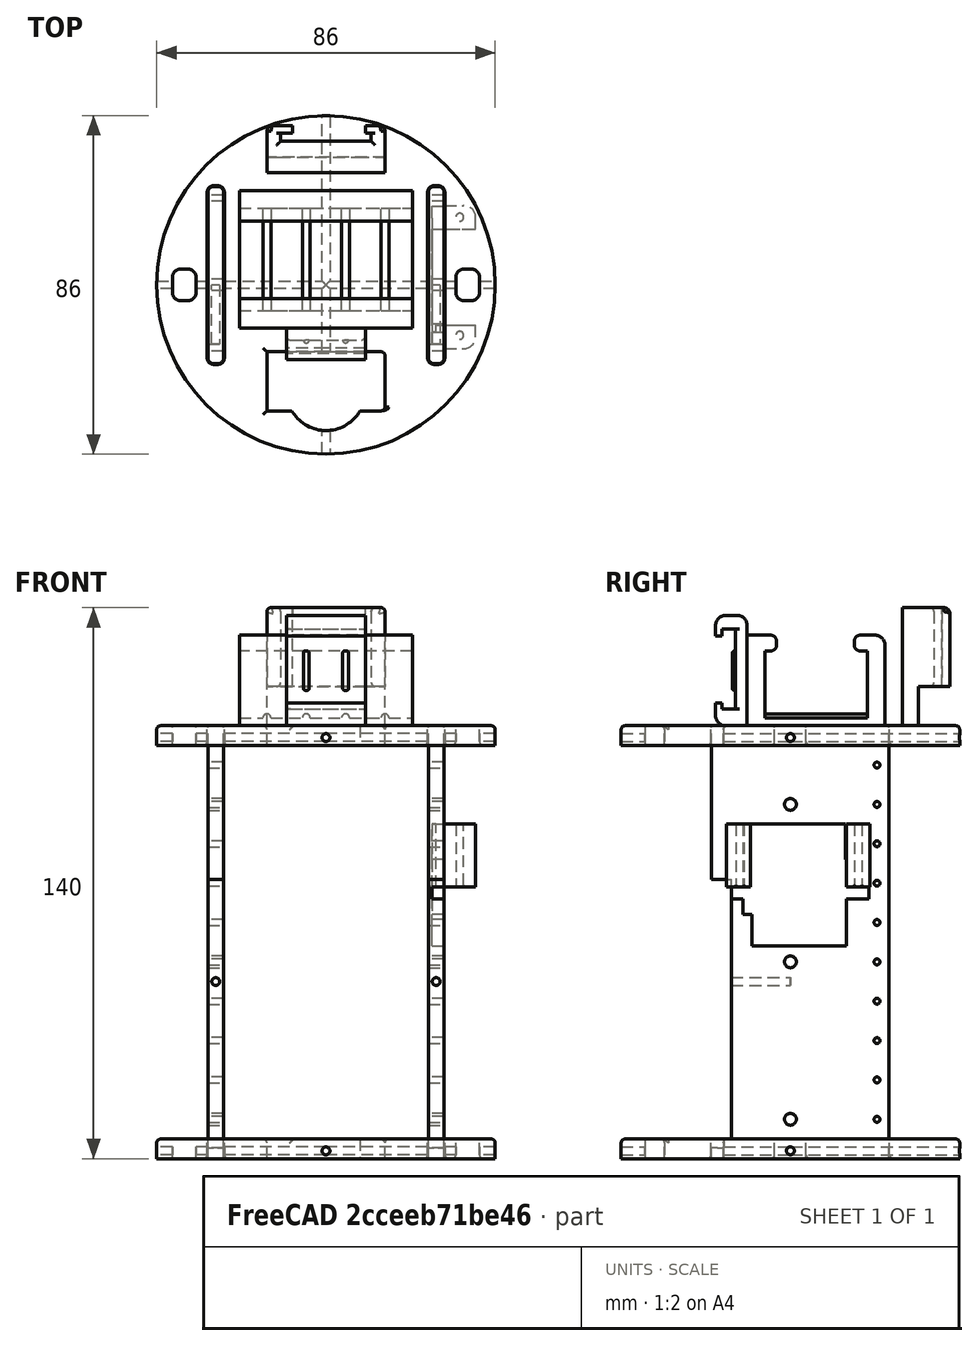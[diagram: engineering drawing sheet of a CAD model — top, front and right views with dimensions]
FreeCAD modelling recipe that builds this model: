
FCSTD DOCUMENT  (FreeCAD 1.0R39109 (Git))
Label: Base_superior_capsula
License: All rights reserved
LicenseURL: http://en.wikipedia.org/wiki/All_rights_reserved
objects: Part::Cut×130, Part::Cylinder×98, Part::Fillet×96, Part::Box×72, Part::MultiFuse×37, Part::Offset×12, Part::Chamfer×1
note: 446 computed .brp shape members not serialized (recipe doc carries the construction recipe); baked Part::Feature solids carry a one-line shape summary decoded from their .brp

FEATURE [Part::Box] Box  label="Extensor"
  AttacherType = Attacher::AttachEngine3D
  Height = 66
  Length = 11
  Placement = pos=(30,-28,3) rot=(0,0,1;1.5708rad)
  Width = 60
FEATURE [Part::Box] Box001  label="Cubo001"
  AttacherType = Attacher::AttachEngine3D
  Height = 110
  Length = 45
  Placement = pos=(-30,25,0) rot=(0,0,-1;1.5708rad)
  Width = 4
FEATURE [Part::Box] Box002  label="Cubo002"
  AttacherType = Attacher::AttachEngine3D
  Height = 110
  Length = 45
  Placement = pos=(-30,25,0) rot=(0,0,-1;1.5708rad)
  Width = 4
FEATURE [Part::Box] Box003  label="Cubo003"
  AttacherType = Attacher::AttachEngine3D
  Height = 10
  Length = 30
  Placement = pos=(-15,-32,0) rot=(0,0,1;0rad)
  Width = 15
FEATURE [Part::Box] Box005  label="Cubo004"
  AttacherType = Attacher::AttachEngine3D
  Height = 15
  Length = 26
  Placement = pos=(-13,-23,110) rot=(0,0,1;0rad)
  Width = 35
FEATURE [Part::Box] Box006  label="Cubo005"
  AttacherType = Attacher::AttachEngine3D
  Height = 150
  Length = 6
  Width = 8
FEATURE [Part::Box] Box007  label="Cubo006"
  AttacherType = Attacher::AttachEngine3D
  Height = 150
  Length = 6
  Width = 8
FEATURE [Part::Box] Box008  label="Cubo007"
  AttacherType = Attacher::AttachEngine3D
  Height = 150
  Length = 6
  Width = 8
FEATURE [Part::Box] Box009  label="Cubo008"
  AttacherType = Attacher::AttachEngine3D
  Height = 150
  Length = 6
  Width = 8
FEATURE [Part::Box] Box010  label="Cubo009"
  AttacherType = Attacher::AttachEngine3D
  Height = 11.6
  Length = 20.8
  Placement = pos=(-10.5,-23,110) rot=(0,0,1;0rad)
  Width = 35
FEATURE [Part::Box] Box011  label="Cubo010"
  AttacherType = Attacher::AttachEngine3D
  Height = 11.6
  Length = 16
  Placement = pos=(-8,-23,116) rot=(0,0,1;0rad)
  Width = 35
FEATURE [Part::Box] Box095  label="Cubo095"
  AttacherType = Attacher::AttachEngine3D
  Height = 110
  Length = 45
  Placement = pos=(-30,25,0) rot=(0,0,-1;1.5708rad)
  Width = 4
FEATURE [Part::Box] Box096  label="Cubo096"
  AttacherType = Attacher::AttachEngine3D
  Height = 110
  Length = 45
  Placement = pos=(-30,25,0) rot=(0,0,-1;1.5708rad)
  Width = 4
FEATURE [Part::Box] Box097  label="Cubo097"
  AttacherType = Attacher::AttachEngine3D
  Height = 23
  Length = 24
  Width = 14
FEATURE [Part::Box] Box098  label="Cubo098"
  AttacherType = Attacher::AttachEngine3D
  Height = 3
  Length = 33.5
  Placement = pos=(-5,0,16) rot=(0,0,1;0rad)
  Width = 14
FEATURE [Part::Box] Box099  label="Cubo099"
  AttacherType = Attacher::AttachEngine3D
  Height = 1.4
  Length = 13
  Placement = pos=(9.8,5,28.6) rot=(0,0,1;0rad)
  Width = 4
FEATURE [Part::Box] Box100  label="Cubo100"
  AttacherType = Attacher::AttachEngine3D
  Height = 16
  Length = 10
  Placement = pos=(28,12.2,69) rot=(0,0,1;0rad)
  Width = 6
FEATURE [Part::Box] Box101  label="Cubo101"
  AttacherType = Attacher::AttachEngine3D
  Height = 16
  Length = 10
  Placement = pos=(28,-18.2,69) rot=(0,0,1;0rad)
  Width = 6
FEATURE [Part::Box] Box102  label="Extensor001"
  AttacherType = Attacher::AttachEngine3D
  Height = 66
  Length = 11
  Placement = pos=(30,-28,3) rot=(0,0,1;1.5708rad)
  Width = 60
FEATURE [Part::Box] Box104  label="Cubo102"
  AttacherType = Attacher::AttachEngine3D
  Height = 8
  Length = 20
  Width = 28
FEATURE [Part::Box] Box105  label="Cubo103"
  AttacherType = Attacher::AttachEngine3D
  Height = 2
  Length = 20.5
  Placement = pos=(0,4,4) rot=(0,0,1;0rad)
  Width = 20.5
FEATURE [Part::Box] Box106  label="Cubo104"
  AttacherType = Attacher::AttachEngine3D
  Height = 4
  Length = 20.5
  Placement = pos=(0,5,5) rot=(0,0,1;0rad)
  Width = 18.5
FEATURE [Part::Box] Box107  label="Cubo105"
  AttacherType = Attacher::AttachEngine3D
  Height = 8
  Length = 20
  Width = 30
FEATURE [Part::Box] Box108  label="Cubo106"
  AttacherType = Attacher::AttachEngine3D
  Height = 2
  Length = 20.5
  Placement = pos=(0,3.5,4) rot=(0,0,1;0rad)
  Width = 23
FEATURE [Part::Box] Box109  label="Cubo107"
  AttacherType = Attacher::AttachEngine3D
  Height = 4
  Length = 20.5
  Placement = pos=(0,5,5) rot=(0,0,1;0rad)
  Width = 18.5
FEATURE [Part::Box] Box110  label="Cubo108"
  AttacherType = Attacher::AttachEngine3D
  Height = 10
  Length = 20
  Placement = pos=(-9,-38,105) rot=(0,0,1;0rad)
  Width = 15
FEATURE [Part::Box] Box111  label="Cubo109"
  AttacherType = Attacher::AttachEngine3D
  Height = 110
  Length = 45
  Placement = pos=(-30,25,0) rot=(0,0,-1;1.5708rad)
  Width = 4
FEATURE [Part::Box] Box112  label="Extensor003"
  AttacherType = Attacher::AttachEngine3D
  Height = 66
  Length = 11
  Placement = pos=(30,-28,3) rot=(0,0,1;1.5708rad)
  Width = 60
FEATURE [Part::Box] Box113  label="Extensor004"
  AttacherType = Attacher::AttachEngine3D
  Height = 66
  Length = 11
  Placement = pos=(30,-28,3) rot=(0,0,1;1.5708rad)
  Width = 60
FEATURE [Part::Box] Box114  label="Cubo110"
  AttacherType = Attacher::AttachEngine3D
  Height = 110
  Length = 45
  Placement = pos=(-30,25,0) rot=(0,0,-1;1.5708rad)
  Width = 4
FEATURE [Part::Box] Box115  label="Cubo111"
  AttacherType = Attacher::AttachEngine3D
  Height = 23
  Length = 24
  Width = 14
FEATURE [Part::Box] Box116  label="Cubo112"
  AttacherType = Attacher::AttachEngine3D
  Height = 3
  Length = 33.5
  Placement = pos=(-5,0,16) rot=(0,0,1;0rad)
  Width = 14
FEATURE [Part::Box] Box117  label="Cubo113"
  AttacherType = Attacher::AttachEngine3D
  Height = 1.4
  Length = 13
  Placement = pos=(9.8,5,28.6) rot=(0,0,1;0rad)
  Width = 4
FEATURE [Part::Box] Box118  label="Cubo114"
  AttacherType = Attacher::AttachEngine3D
  Height = 16
  Length = 10
  Placement = pos=(28,12.2,69) rot=(0,0,1;0rad)
  Width = 6
FEATURE [Part::Box] Box119  label="Cubo115"
  AttacherType = Attacher::AttachEngine3D
  Height = 16
  Length = 10
  Placement = pos=(28,-18.2,69) rot=(0,0,1;0rad)
  Width = 6
FEATURE [Part::Box] Box120  label="Cubo116"
  AttacherType = Attacher::AttachEngine3D
  Height = 10
  Length = 4
  Placement = pos=(-30,-20,0) rot=(0,0,1;0rad)
  Width = 45
FEATURE [Part::Box] Box121  label="Cubo117"
  AttacherType = Attacher::AttachEngine3D
  Height = 10
  Length = 4
  Placement = pos=(-30,-20,0) rot=(0,0,1;0rad)
  Width = 45
FEATURE [Part::Box] Box122  label="Cubo118"
  AttacherType = Attacher::AttachEngine3D
  Height = 8
  Length = 20
  Width = 30
FEATURE [Part::Box] Box123  label="Cubo119"
  AttacherType = Attacher::AttachEngine3D
  Height = 2
  Length = 20.5
  Placement = pos=(0,3.5,4) rot=(0,0,1;0rad)
  Width = 23
FEATURE [Part::Box] Box124  label="Cubo120"
  AttacherType = Attacher::AttachEngine3D
  Height = 4
  Length = 20.5
  Placement = pos=(0,5,5) rot=(0,0,1;0rad)
  Width = 18.5
FEATURE [Part::Box] Box128  label="Cubo124"
  AttacherType = Attacher::AttachEngine3D
  Height = 30
  Length = 33
  Placement = pos=(-16,-43,115) rot=(0,0,1;0rad)
  Width = 30
FEATURE [Part::Box] Box129  label="Cubo125"
  AttacherType = Attacher::AttachEngine3D
  Height = 30
  Length = 33
  Placement = pos=(-16,13,110) rot=(0,0,1;0rad)
  Width = 30
FEATURE [Part::Box] Box130  label="Cubo126"
  AttacherType = Attacher::AttachEngine3D
  Height = 30
  Length = 30
  Placement = pos=(-16,13,110) rot=(0,0,1;0rad)
  Width = 4
FEATURE [Part::Box] Box131  label="Cubo127"
  AttacherType = Attacher::AttachEngine3D
  Height = 3.4
  Length = 21
  Placement = pos=(0,4.2,3) rot=(0,0,1;0rad)
  Width = 20.4
FEATURE [Part::Box] Box132  label="Cubo128"
  AttacherType = Attacher::AttachEngine3D
  Height = 4
  Length = 21
  Placement = pos=(0,5.75,6) rot=(0,0,1;0rad)
  Width = 17
FEATURE [Part::Box] Box133  label="Cubo129"
  AttacherType = Attacher::AttachEngine3D
  Height = 8
  Length = 20
  Width = 28
FEATURE [Part::Box] Box134  label="Cubo130"
  AttacherType = Attacher::AttachEngine3D
  Height = 16
  Length = 37
  Placement = pos=(-19,-15,110) rot=(0,0,1;0rad)
  Width = 30
FEATURE [Part::Box] Box135  label="Pila_ext"
  AttacherType = Attacher::AttachEngine3D
  Height = 25
  Length = 44
  Placement = pos=(-22,-11,110) rot=(0,0,1;0rad)
  Width = 35
FEATURE [Part::Box] Box136  label="Pila_int"
  AttacherType = Attacher::AttachEngine3D
  Height = 17
  Length = 44
  Placement = pos=(-22,-6.5,114) rot=(0,0,1;0rad)
  Width = 26
FEATURE [Part::Box] Box137  label="hueco_pila"
  AttacherType = Attacher::AttachEngine3D
  Height = 16.65
  Length = 44
  Placement = pos=(-22,-3.5,122) rot=(0,0,1;0rad)
  Width = 19.72
FEATURE [Part::Box] Box165  label="Cubo155"
  AttacherType = Attacher::AttachEngine3D
  Height = 17
  Length = 19
  Placement = pos=(27,-9.8,59) rot=(0,0,1;0rad)
  Width = 24
FEATURE [Part::Box] Box166  label="Cubo156"
  AttacherType = Attacher::AttachEngine3D
  Height = 66
  Length = 60
  Placement = pos=(-30,-20,5) rot=(0,0,1;0rad)
  Width = 5
FEATURE [Part::Box] Box167  label="Cubo157"
  AttacherType = Attacher::AttachEngine3D
  Height = 66
  Length = 60
  Placement = pos=(-30,-20,5) rot=(0,0,1;0rad)
  Width = 5
FEATURE [Part::Box] Box168  label="Cubo158"
  AttacherType = Attacher::AttachEngine3D
  Height = 3
  Length = 4
  Placement = pos=(27,7,66) rot=(0,0,1;0rad)
  Width = 13
FEATURE [Part::Box] Box169  label="Cubo159"
  AttacherType = Attacher::AttachEngine3D
  Height = 3
  Length = 4
  Placement = pos=(27,-9.8,56) rot=(0,0,1;0rad)
  Width = 24
FEATURE [Part::Box] Box170  label="Cubo160"
  AttacherType = Attacher::AttachEngine3D
  Height = 10
  Length = 30
  Placement = pos=(-15,-32,0) rot=(0,0,1;0rad)
  Width = 15
FEATURE [Part::Box] Box171  label="Cubo161"
  AttacherType = Attacher::AttachEngine3D
  Height = 150
  Length = 6
  Width = 8
FEATURE [Part::Box] Box172  label="Cubo162"
  AttacherType = Attacher::AttachEngine3D
  Height = 150
  Length = 6
  Width = 8
FEATURE [Part::Box] Box173  label="Cubo163"
  AttacherType = Attacher::AttachEngine3D
  Height = 110
  Length = 45
  Placement = pos=(-30,25,0) rot=(0,0,-1;1.5708rad)
  Width = 4
FEATURE [Part::Box] Box174  label="Extensor005"
  AttacherType = Attacher::AttachEngine3D
  Height = 66
  Length = 11
  Placement = pos=(30,-28,3) rot=(0,0,1;1.5708rad)
  Width = 60
FEATURE [Part::Box] Box175  label="Extensor006"
  AttacherType = Attacher::AttachEngine3D
  Height = 66
  Length = 11
  Placement = pos=(30,-28,3) rot=(0,0,1;1.5708rad)
  Width = 60
FEATURE [Part::Box] Box176  label="Cubo164"
  AttacherType = Attacher::AttachEngine3D
  Height = 110
  Length = 45
  Placement = pos=(-30,25,0) rot=(0,0,-1;1.5708rad)
  Width = 4
FEATURE [Part::Box] Box177  label="Cubo165"
  AttacherType = Attacher::AttachEngine3D
  Height = 23
  Length = 24
  Width = 14
FEATURE [Part::Box] Box178  label="Cubo166"
  AttacherType = Attacher::AttachEngine3D
  Height = 3
  Length = 33.5
  Placement = pos=(-5,0,16) rot=(0,0,1;0rad)
  Width = 14
FEATURE [Part::Box] Box179  label="Cubo167"
  AttacherType = Attacher::AttachEngine3D
  Height = 1.4
  Length = 13
  Placement = pos=(9.8,5,28.6) rot=(0,0,1;0rad)
  Width = 4
FEATURE [Part::Box] Box180  label="Cubo168"
  AttacherType = Attacher::AttachEngine3D
  Height = 16
  Length = 10
  Placement = pos=(28,12.2,69) rot=(0,0,1;0rad)
  Width = 6
FEATURE [Part::Box] Box181  label="Cubo169"
  AttacherType = Attacher::AttachEngine3D
  Height = 16
  Length = 10
  Placement = pos=(28,-18.2,69) rot=(0,0,1;0rad)
  Width = 6
FEATURE [Part::Box] Box182  label="Cubo170"
  AttacherType = Attacher::AttachEngine3D
  Height = 10
  Length = 4
  Placement = pos=(-30,-20,0) rot=(0,0,1;0rad)
  Width = 45
FEATURE [Part::Box] Box183  label="Cubo171"
  AttacherType = Attacher::AttachEngine3D
  Height = 10
  Length = 4
  Placement = pos=(-30,-20,0) rot=(0,0,1;0rad)
  Width = 45
FEATURE [Part::Box] Box184  label="Cubo172"
  AttacherType = Attacher::AttachEngine3D
  Height = 10
  Length = 120
  Placement = pos=(-50,-47,100) rot=(0,0,1;0rad)
  Width = 120
FEATURE [Part::Box] Box197  label="Cubo184"
  AttacherType = Attacher::AttachEngine3D
  Height = 16
  Length = 3
  Placement = pos=(27,12,69) rot=(0,0,1;0rad)
  Width = 2
FEATURE [Part::Box] Box198  label="Cubo185"
  AttacherType = Attacher::AttachEngine3D
  Height = 24
  Length = 3
  Placement = pos=(27,14.2,54) rot=(1,0,0;1.5708rad)
  Width = 4
FEATURE [Part::Cut] Cut016
  Base = -> Box005
  Tool = -> Box010
FEATURE [Part::Cut] Cut017
  Base = -> Cut016
  Placement = pos=(-5,0,0) rot=(0,0,1;1.5708rad)
  Tool = -> Box011
FEATURE [Part::Cut] Cut115
  Base = -> Box104
  Tool = -> Box105
FEATURE [Part::Cut] Cut116
  Base = -> Cut115
  Tool = -> Box106
FEATURE [Part::Cut] Cut117
  Base = -> Box107
  Tool = -> Box108
FEATURE [Part::Cut] Cut118
  Base = -> Cut117
  Tool = -> Box109
FEATURE [Part::Cut] Cut143
  Base = -> Box122
  Tool = -> Box123
FEATURE [Part::Cut] Cut144
  Base = -> Cut143
  Tool = -> Box124
FEATURE [Part::Cut] Cut149
  Base = -> Box133
  Tool = -> Box131
FEATURE [Part::Cut] Cut150
  Base = -> Cut149
  Tool = -> Box132
FEATURE [Part::Cut] Cut152
  Base = -> Box135
  Tool = -> Box136
FEATURE [Part::Cut] Cut153  label="PortaPIlas_9V"
  Base = -> Cut152
  Placement = pos=(0,0,-2) rot=(0,0,1;0rad)
  Tool = -> Box137
FEATURE [Part::Cylinder] Cylinder  label="Cilindro"
  Angle = 360
  AttacherType = Attacher::AttachEngine3D
  FirstAngle = 0
  Height = 5
  Radius = 43
  SecondAngle = 0
FEATURE [Part::Cylinder] Cylinder002  label="Cilindro002"
  Angle = 360
  AttacherType = Attacher::AttachEngine3D
  FirstAngle = 0
  Height = 20
  Placement = pos=(0,44,1.5) rot=(1,0,0;1.5708rad)
  Radius = 0.5
  SecondAngle = 0
FEATURE [Part::Cylinder] Cylinder003  label="Cilindro003"
  Angle = 360
  AttacherType = Attacher::AttachEngine3D
  FirstAngle = 0
  Height = 20
  Placement = pos=(0,-26,1.5) rot=(1,0,0;1.5708rad)
  Radius = 0.5
  SecondAngle = 0
FEATURE [Part::Cylinder] Cylinder004  label="Cilindro004"
  Angle = 360
  AttacherType = Attacher::AttachEngine3D
  FirstAngle = 0
  Height = 3
  Radius = 43
  SecondAngle = 0
FEATURE [Part::Cylinder] Cylinder005  label="Cilindro005"
  Angle = 360
  AttacherType = Attacher::AttachEngine3D
  FirstAngle = 0
  Height = 20
  Placement = pos=(0,44,1.5) rot=(1,0,0;1.5708rad)
  Radius = 0.5
  SecondAngle = 0
FEATURE [Part::Cylinder] Cylinder006  label="Cilindro006"
  Angle = 360
  AttacherType = Attacher::AttachEngine3D
  FirstAngle = 0
  Height = 20
  Placement = pos=(0,-26,1.5) rot=(1,0,0;1.5708rad)
  Radius = 0.5
  SecondAngle = 0
FEATURE [Part::Cylinder] Cylinder008  label="Cilindro008"
  Angle = 360
  AttacherType = Attacher::AttachEngine3D
  FirstAngle = 0
  Height = 100
  Placement = pos=(-46,0,50) rot=(0,1,0;1.5708rad)
  Radius = 1.5
  SecondAngle = 0
FEATURE [Part::Cylinder] Cylinder009  label="Cilindro009"
  Angle = 360
  AttacherType = Attacher::AttachEngine3D
  FirstAngle = 0
  Height = 100
  Placement = pos=(-46,0,90) rot=(0,1,0;1.5708rad)
  Radius = 1.5
  SecondAngle = 0
FEATURE [Part::Cylinder] Cylinder010  label="Cilindro010"
  Angle = 360
  AttacherType = Attacher::AttachEngine3D
  FirstAngle = 0
  Height = 100
  Placement = pos=(-46,0,10) rot=(0,1,0;1.5708rad)
  Radius = 1.5
  SecondAngle = 0
FEATURE [Part::Cylinder] Cylinder011  label="Cilindro011"
  Angle = 360
  AttacherType = Attacher::AttachEngine3D
  FirstAngle = 0
  Height = 10
  Placement = pos=(0,-27,0) rot=(0,0,1;0rad)
  Radius = 10
  SecondAngle = 0
FEATURE [Part::Cylinder] Cylinder071  label="Cilindro071"
  Angle = 360
  AttacherType = Attacher::AttachEngine3D
  FirstAngle = 0
  Height = 100
  Placement = pos=(-46,0,50) rot=(0,1,0;1.5708rad)
  Radius = 1.5
  SecondAngle = 0
FEATURE [Part::Cylinder] Cylinder072  label="Cilindro072"
  Angle = 360
  AttacherType = Attacher::AttachEngine3D
  FirstAngle = 0
  Height = 100
  Placement = pos=(-46,0,90) rot=(0,1,0;1.5708rad)
  Radius = 1.5
  SecondAngle = 0
FEATURE [Part::Cylinder] Cylinder073  label="Cilindro073"
  Angle = 360
  AttacherType = Attacher::AttachEngine3D
  FirstAngle = 0
  Height = 100
  Placement = pos=(-46,0,10) rot=(0,1,0;1.5708rad)
  Radius = 1.5
  SecondAngle = 0
FEATURE [Part::Cylinder] Cylinder074  label="Cilindro074"
  Angle = 360
  AttacherType = Attacher::AttachEngine3D
  FirstAngle = 0
  Height = 3
  Placement = pos=(7,7,23) rot=(0,0,1;0rad)
  Radius = 7
  SecondAngle = 0
FEATURE [Part::Cylinder] Cylinder075  label="Cilindro075"
  Angle = 360
  AttacherType = Attacher::AttachEngine3D
  FirstAngle = 0
  Height = 3
  Placement = pos=(14,7,23) rot=(0,0,1;0rad)
  Radius = 2
  SecondAngle = 0
FEATURE [Part::Cylinder] Cylinder076  label="Cilindro076"
  Angle = 360
  AttacherType = Attacher::AttachEngine3D
  FirstAngle = 0
  Height = 10
  Placement = pos=(-3.2,7,12) rot=(0,0,1;0rad)
  Radius = 1.65
  SecondAngle = 0
FEATURE [Part::Cylinder] Cylinder077  label="Cilindro077"
  Angle = 360
  AttacherType = Attacher::AttachEngine3D
  FirstAngle = 0
  Height = 10
  Placement = pos=(26.8,7,12) rot=(0,0,1;0rad)
  Radius = 1.65
  SecondAngle = 0
FEATURE [Part::Cylinder] Cylinder078  label="Cilindro078"
  Angle = 360
  AttacherType = Attacher::AttachEngine3D
  FirstAngle = 0
  Height = 4
  Placement = pos=(7,7,26) rot=(0,0,1;0rad)
  Radius = 3.5
  SecondAngle = 0
FEATURE [Part::Cylinder] Cylinder079  label="Cilindro079"
  Angle = 360
  AttacherType = Attacher::AttachEngine3D
  FirstAngle = 0
  Height = 10
  Placement = pos=(21,7,25) rot=(0,0,1;0rad)
  Radius = 0.25
  SecondAngle = 0
FEATURE [Part::Cylinder] Cylinder080  label="Cilindro080"
  Angle = 360
  AttacherType = Attacher::AttachEngine3D
  FirstAngle = 0
  Height = 10
  Placement = pos=(19,7,25) rot=(0,0,1;0rad)
  Radius = 0.25
  SecondAngle = 0
FEATURE [Part::Cylinder] Cylinder081  label="Cilindro081"
  Angle = 360
  AttacherType = Attacher::AttachEngine3D
  FirstAngle = 0
  Height = 10
  Placement = pos=(17,7,25) rot=(0,0,1;0rad)
  Radius = 0.25
  SecondAngle = 0
FEATURE [Part::Cylinder] Cylinder082  label="Cilindro082"
  Angle = 360
  AttacherType = Attacher::AttachEngine3D
  FirstAngle = 0
  Height = 10
  Placement = pos=(15,7,27) rot=(0,0,1;0rad)
  Radius = 0.25
  SecondAngle = 0
FEATURE [Part::Cylinder] Cylinder083  label="Cilindro083"
  Angle = 360
  AttacherType = Attacher::AttachEngine3D
  FirstAngle = 0
  Height = 10
  Placement = pos=(13,7,27) rot=(0,0,1;0rad)
  Radius = 0.25
  SecondAngle = 0
FEATURE [Part::Cylinder] Cylinder084  label="Cilindro084"
  Angle = 360
  AttacherType = Attacher::AttachEngine3D
  FirstAngle = 0
  Height = 20
  Placement = pos=(34,-14.8,66) rot=(0,0,1;0rad)
  Radius = 1
  SecondAngle = 0
FEATURE [Part::Cylinder] Cylinder085  label="Cilindro085"
  Angle = 360
  AttacherType = Attacher::AttachEngine3D
  FirstAngle = 0
  Height = 20
  Placement = pos=(34,15.2,66) rot=(0,0,1;0rad)
  Radius = 1
  SecondAngle = 0
FEATURE [Part::Cylinder] Cylinder086  label="Cilindro086"
  Angle = 360
  AttacherType = Attacher::AttachEngine3D
  FirstAngle = 0
  Height = 100
  Placement = pos=(-46,0,50) rot=(0,1,0;1.5708rad)
  Radius = 1.5
  SecondAngle = 0
FEATURE [Part::Cylinder] Cylinder087  label="Cilindro087"
  Angle = 360
  AttacherType = Attacher::AttachEngine3D
  FirstAngle = 0
  Height = 100
  Placement = pos=(-46,0,90) rot=(0,1,0;1.5708rad)
  Radius = 1.5
  SecondAngle = 0
FEATURE [Part::Cylinder] Cylinder088  label="Cilindro088"
  Angle = 360
  AttacherType = Attacher::AttachEngine3D
  FirstAngle = 0
  Height = 100
  Placement = pos=(-46,0,10) rot=(0,1,0;1.5708rad)
  Radius = 1.5
  SecondAngle = 0
FEATURE [Part::Cylinder] Cylinder089  label="Cilindro089"
  Angle = 360
  AttacherType = Attacher::AttachEngine3D
  FirstAngle = 0
  Height = 100
  Placement = pos=(-46,0,50) rot=(0,1,0;1.5708rad)
  Radius = 1.5
  SecondAngle = 0
FEATURE [Part::Cylinder] Cylinder090  label="Cilindro090"
  Angle = 360
  AttacherType = Attacher::AttachEngine3D
  FirstAngle = 0
  Height = 100
  Placement = pos=(-46,0,90) rot=(0,1,0;1.5708rad)
  Radius = 1.5
  SecondAngle = 0
FEATURE [Part::Cylinder] Cylinder091  label="Cilindro091"
  Angle = 360
  AttacherType = Attacher::AttachEngine3D
  FirstAngle = 0
  Height = 100
  Placement = pos=(-46,0,10) rot=(0,1,0;1.5708rad)
  Radius = 1.5
  SecondAngle = 0
FEATURE [Part::Cylinder] Cylinder092  label="Cilindro092"
  Angle = 360
  AttacherType = Attacher::AttachEngine3D
  FirstAngle = 0
  Height = 3
  Placement = pos=(7,7,23) rot=(0,0,1;0rad)
  Radius = 7
  SecondAngle = 0
FEATURE [Part::Cylinder] Cylinder093  label="Cilindro093"
  Angle = 360
  AttacherType = Attacher::AttachEngine3D
  FirstAngle = 0
  Height = 3
  Placement = pos=(14,7,23) rot=(0,0,1;0rad)
  Radius = 2
  SecondAngle = 0
FEATURE [Part::Cylinder] Cylinder094  label="Cilindro094"
  Angle = 360
  AttacherType = Attacher::AttachEngine3D
  FirstAngle = 0
  Height = 10
  Placement = pos=(-3.2,7,12) rot=(0,0,1;0rad)
  Radius = 1.65
  SecondAngle = 0
FEATURE [Part::Cylinder] Cylinder095  label="Cilindro095"
  Angle = 360
  AttacherType = Attacher::AttachEngine3D
  FirstAngle = 0
  Height = 10
  Placement = pos=(26.8,7,12) rot=(0,0,1;0rad)
  Radius = 1.65
  SecondAngle = 0
FEATURE [Part::Cylinder] Cylinder096  label="Cilindro096"
  Angle = 360
  AttacherType = Attacher::AttachEngine3D
  FirstAngle = 0
  Height = 4
  Placement = pos=(7,7,26) rot=(0,0,1;0rad)
  Radius = 3.5
  SecondAngle = 0
FEATURE [Part::Cylinder] Cylinder097  label="Cilindro097"
  Angle = 360
  AttacherType = Attacher::AttachEngine3D
  FirstAngle = 0
  Height = 10
  Placement = pos=(21,7,25) rot=(0,0,1;0rad)
  Radius = 0.25
  SecondAngle = 0
FEATURE [Part::Cylinder] Cylinder098  label="Cilindro098"
  Angle = 360
  AttacherType = Attacher::AttachEngine3D
  FirstAngle = 0
  Height = 10
  Placement = pos=(19,7,25) rot=(0,0,1;0rad)
  Radius = 0.25
  SecondAngle = 0
FEATURE [Part::Cylinder] Cylinder099  label="Cilindro099"
  Angle = 360
  AttacherType = Attacher::AttachEngine3D
  FirstAngle = 0
  Height = 10
  Placement = pos=(17,7,25) rot=(0,0,1;0rad)
  Radius = 0.25
  SecondAngle = 0
FEATURE [Part::Cylinder] Cylinder100  label="Cilindro100"
  Angle = 360
  AttacherType = Attacher::AttachEngine3D
  FirstAngle = 0
  Height = 10
  Placement = pos=(15,7,27) rot=(0,0,1;0rad)
  Radius = 0.25
  SecondAngle = 0
FEATURE [Part::Cylinder] Cylinder101  label="Cilindro101"
  Angle = 360
  AttacherType = Attacher::AttachEngine3D
  FirstAngle = 0
  Height = 10
  Placement = pos=(13,7,27) rot=(0,0,1;0rad)
  Radius = 0.25
  SecondAngle = 0
FEATURE [Part::Cylinder] Cylinder102  label="Cilindro102"
  Angle = 360
  AttacherType = Attacher::AttachEngine3D
  FirstAngle = 0
  Height = 20
  Placement = pos=(34,-14.8,66) rot=(0,0,1;0rad)
  Radius = 1
  SecondAngle = 0
FEATURE [Part::Cylinder] Cylinder103  label="Cilindro103"
  Angle = 360
  AttacherType = Attacher::AttachEngine3D
  FirstAngle = 0
  Height = 20
  Placement = pos=(34,15.2,66) rot=(0,0,1;0rad)
  Radius = 1
  SecondAngle = 0
FEATURE [Part::Cylinder] Cylinder104  label="Cilindro104"
  Angle = 360
  AttacherType = Attacher::AttachEngine3D
  FirstAngle = 0
  Height = 100
  Placement = pos=(0,52,2) rot=(1,0,0;1.5708rad)
  Radius = 1
  SecondAngle = 0
FEATURE [Part::Cylinder] Cylinder109  label="Cilindro109"
  Angle = 360
  AttacherType = Attacher::AttachEngine3D
  FirstAngle = 0
  Height = 15
  Placement = pos=(-28,0,45) rot=(1,0,0;1.5708rad)
  Radius = 1
  SecondAngle = 0
FEATURE [Part::Cylinder] Cylinder110  label="Cilindro110"
  Angle = 360
  AttacherType = Attacher::AttachEngine3D
  FirstAngle = 0
  Height = 15
  Placement = pos=(28,0,45) rot=(1,0,0;1.5708rad)
  Radius = 1
  SecondAngle = 0
FEATURE [Part::Cylinder] Cylinder111  label="Cilindro111"
  Angle = 360
  AttacherType = Attacher::AttachEngine3D
  FirstAngle = 0
  Height = 67
  Placement = pos=(-33,22,10) rot=(0,1,0;1.5708rad)
  Radius = 0.75
  SecondAngle = 0
FEATURE [Part::Cylinder] Cylinder112  label="Cilindro112"
  Angle = 360
  AttacherType = Attacher::AttachEngine3D
  FirstAngle = 0
  Height = 67
  Placement = pos=(-33,22,100) rot=(0,1,0;1.5708rad)
  Radius = 0.75
  SecondAngle = 0
FEATURE [Part::Cylinder] Cylinder113  label="Cilindro113"
  Angle = 360
  AttacherType = Attacher::AttachEngine3D
  FirstAngle = 0
  Height = 67
  Placement = pos=(-33,22,20) rot=(0,1,0;1.5708rad)
  Radius = 0.75
  SecondAngle = 0
FEATURE [Part::Cylinder] Cylinder114  label="Cilindro114"
  Angle = 360
  AttacherType = Attacher::AttachEngine3D
  FirstAngle = 0
  Height = 67
  Placement = pos=(-33,22,30) rot=(0,1,0;1.5708rad)
  Radius = 0.75
  SecondAngle = 0
FEATURE [Part::Cylinder] Cylinder115  label="Cilindro115"
  Angle = 360
  AttacherType = Attacher::AttachEngine3D
  FirstAngle = 0
  Height = 67
  Placement = pos=(-33,22,40) rot=(0,1,0;1.5708rad)
  Radius = 0.75
  SecondAngle = 0
FEATURE [Part::Cylinder] Cylinder116  label="Cilindro116"
  Angle = 360
  AttacherType = Attacher::AttachEngine3D
  FirstAngle = 0
  Height = 67
  Placement = pos=(-33,22,50) rot=(0,1,0;1.5708rad)
  Radius = 0.75
  SecondAngle = 0
FEATURE [Part::Cylinder] Cylinder117  label="Cilindro117"
  Angle = 360
  AttacherType = Attacher::AttachEngine3D
  FirstAngle = 0
  Height = 67
  Placement = pos=(-33,22,60) rot=(0,1,0;1.5708rad)
  Radius = 0.75
  SecondAngle = 0
FEATURE [Part::Cylinder] Cylinder118  label="Cilindro118"
  Angle = 360
  AttacherType = Attacher::AttachEngine3D
  FirstAngle = 0
  Height = 67
  Placement = pos=(-33,22,70) rot=(0,1,0;1.5708rad)
  Radius = 0.75
  SecondAngle = 0
FEATURE [Part::Cylinder] Cylinder119  label="Cilindro119"
  Angle = 360
  AttacherType = Attacher::AttachEngine3D
  FirstAngle = 0
  Height = 67
  Placement = pos=(-33,22,80) rot=(0,1,0;1.5708rad)
  Radius = 0.75
  SecondAngle = 0
FEATURE [Part::Cylinder] Cylinder120  label="Cilindro120"
  Angle = 360
  AttacherType = Attacher::AttachEngine3D
  FirstAngle = 0
  Height = 67
  Placement = pos=(-33,22,90) rot=(0,1,0;1.5708rad)
  Radius = 0.75
  SecondAngle = 0
FEATURE [Part::Cylinder] Cylinder121  label="Cilindro121"
  Angle = 360
  AttacherType = Attacher::AttachEngine3D
  FirstAngle = 0
  Height = 67
  Placement = pos=(-33,22,10) rot=(0,1,0;1.5708rad)
  Radius = 0.75
  SecondAngle = 0
FEATURE [Part::Cylinder] Cylinder122  label="Cilindro122"
  Angle = 360
  AttacherType = Attacher::AttachEngine3D
  FirstAngle = 0
  Height = 67
  Placement = pos=(-33,22,100) rot=(0,1,0;1.5708rad)
  Radius = 0.75
  SecondAngle = 0
FEATURE [Part::Cylinder] Cylinder123  label="Cilindro123"
  Angle = 360
  AttacherType = Attacher::AttachEngine3D
  FirstAngle = 0
  Height = 67
  Placement = pos=(-33,22,20) rot=(0,1,0;1.5708rad)
  Radius = 0.75
  SecondAngle = 0
FEATURE [Part::Cylinder] Cylinder124  label="Cilindro124"
  Angle = 360
  AttacherType = Attacher::AttachEngine3D
  FirstAngle = 0
  Height = 67
  Placement = pos=(-33,22,30) rot=(0,1,0;1.5708rad)
  Radius = 0.75
  SecondAngle = 0
FEATURE [Part::Cylinder] Cylinder125  label="Cilindro125"
  Angle = 360
  AttacherType = Attacher::AttachEngine3D
  FirstAngle = 0
  Height = 67
  Placement = pos=(-33,22,40) rot=(0,1,0;1.5708rad)
  Radius = 0.75
  SecondAngle = 0
FEATURE [Part::Cylinder] Cylinder126  label="Cilindro126"
  Angle = 360
  AttacherType = Attacher::AttachEngine3D
  FirstAngle = 0
  Height = 67
  Placement = pos=(-33,22,50) rot=(0,1,0;1.5708rad)
  Radius = 0.75
  SecondAngle = 0
FEATURE [Part::Cylinder] Cylinder127  label="Cilindro127"
  Angle = 360
  AttacherType = Attacher::AttachEngine3D
  FirstAngle = 0
  Height = 67
  Placement = pos=(-33,22,60) rot=(0,1,0;1.5708rad)
  Radius = 0.75
  SecondAngle = 0
FEATURE [Part::Cylinder] Cylinder128  label="Cilindro128"
  Angle = 360
  AttacherType = Attacher::AttachEngine3D
  FirstAngle = 0
  Height = 67
  Placement = pos=(-33,22,70) rot=(0,1,0;1.5708rad)
  Radius = 0.75
  SecondAngle = 0
FEATURE [Part::Cylinder] Cylinder129  label="Cilindro129"
  Angle = 360
  AttacherType = Attacher::AttachEngine3D
  FirstAngle = 0
  Height = 67
  Placement = pos=(-33,22,80) rot=(0,1,0;1.5708rad)
  Radius = 0.75
  SecondAngle = 0
FEATURE [Part::Cylinder] Cylinder130  label="Cilindro130"
  Angle = 360
  AttacherType = Attacher::AttachEngine3D
  FirstAngle = 0
  Height = 67
  Placement = pos=(-33,22,90) rot=(0,1,0;1.5708rad)
  Radius = 0.75
  SecondAngle = 0
FEATURE [Part::Cylinder] Cylinder131  label="Cilindro131"
  Angle = 360
  AttacherType = Attacher::AttachEngine3D
  FirstAngle = 0
  Height = 67
  Placement = pos=(-33,22,70) rot=(0,1,0;1.5708rad)
  Radius = 0.75
  SecondAngle = 0
FEATURE [Part::Cylinder] Cylinder133  label="Cilindro133"
  Angle = 360
  AttacherType = Attacher::AttachEngine3D
  FirstAngle = 0
  Height = 110
  Placement = pos=(-55,0,2) rot=(0.57735,0.57735,0.57735;2.0944rad)
  Radius = 1
  SecondAngle = 0
FEATURE [Part::Cylinder] Cylinder134  label="Cilindro134"
  Angle = 360
  AttacherType = Attacher::AttachEngine3D
  FirstAngle = 0
  Height = 5
  Radius = 43
  SecondAngle = 0
FEATURE [Part::Cylinder] Cylinder135  label="Cilindro135"
  Angle = 360
  AttacherType = Attacher::AttachEngine3D
  FirstAngle = 0
  Height = 20
  Placement = pos=(0,44,1.5) rot=(1,0,0;1.5708rad)
  Radius = 0.5
  SecondAngle = 0
FEATURE [Part::Cylinder] Cylinder136  label="Cilindro136"
  Angle = 360
  AttacherType = Attacher::AttachEngine3D
  FirstAngle = 0
  Height = 20
  Placement = pos=(0,-26,1.5) rot=(1,0,0;1.5708rad)
  Radius = 0.5
  SecondAngle = 0
FEATURE [Part::Cylinder] Cylinder137  label="Cilindro137"
  Angle = 360
  AttacherType = Attacher::AttachEngine3D
  FirstAngle = 0
  Height = 10
  Placement = pos=(0,-27,0) rot=(0,0,1;0rad)
  Radius = 10
  SecondAngle = 0
FEATURE [Part::Cylinder] Cylinder138  label="Cilindro138"
  Angle = 360
  AttacherType = Attacher::AttachEngine3D
  FirstAngle = 0
  Height = 100
  Placement = pos=(-46,0,50) rot=(0,1,0;1.5708rad)
  Radius = 1.5
  SecondAngle = 0
FEATURE [Part::Cylinder] Cylinder139  label="Cilindro139"
  Angle = 360
  AttacherType = Attacher::AttachEngine3D
  FirstAngle = 0
  Height = 100
  Placement = pos=(-46,0,90) rot=(0,1,0;1.5708rad)
  Radius = 1.5
  SecondAngle = 0
FEATURE [Part::Cylinder] Cylinder140  label="Cilindro140"
  Angle = 360
  AttacherType = Attacher::AttachEngine3D
  FirstAngle = 0
  Height = 100
  Placement = pos=(-46,0,10) rot=(0,1,0;1.5708rad)
  Radius = 1.5
  SecondAngle = 0
FEATURE [Part::Cylinder] Cylinder141  label="Cilindro141"
  Angle = 360
  AttacherType = Attacher::AttachEngine3D
  FirstAngle = 0
  Height = 100
  Placement = pos=(-46,0,50) rot=(0,1,0;1.5708rad)
  Radius = 1.5
  SecondAngle = 0
FEATURE [Part::Cylinder] Cylinder142  label="Cilindro142"
  Angle = 360
  AttacherType = Attacher::AttachEngine3D
  FirstAngle = 0
  Height = 100
  Placement = pos=(-46,0,90) rot=(0,1,0;1.5708rad)
  Radius = 1.5
  SecondAngle = 0
FEATURE [Part::Cylinder] Cylinder143  label="Cilindro143"
  Angle = 360
  AttacherType = Attacher::AttachEngine3D
  FirstAngle = 0
  Height = 100
  Placement = pos=(-46,0,10) rot=(0,1,0;1.5708rad)
  Radius = 1.5
  SecondAngle = 0
FEATURE [Part::Cylinder] Cylinder144  label="Cilindro144"
  Angle = 360
  AttacherType = Attacher::AttachEngine3D
  FirstAngle = 0
  Height = 3
  Placement = pos=(7,7,23) rot=(0,0,1;0rad)
  Radius = 7
  SecondAngle = 0
FEATURE [Part::Cylinder] Cylinder145  label="Cilindro145"
  Angle = 360
  AttacherType = Attacher::AttachEngine3D
  FirstAngle = 0
  Height = 3
  Placement = pos=(14,7,23) rot=(0,0,1;0rad)
  Radius = 2
  SecondAngle = 0
FEATURE [Part::Cylinder] Cylinder146  label="Cilindro146"
  Angle = 360
  AttacherType = Attacher::AttachEngine3D
  FirstAngle = 0
  Height = 10
  Placement = pos=(-3.2,7,12) rot=(0,0,1;0rad)
  Radius = 1.65
  SecondAngle = 0
FEATURE [Part::Cylinder] Cylinder147  label="Cilindro147"
  Angle = 360
  AttacherType = Attacher::AttachEngine3D
  FirstAngle = 0
  Height = 10
  Placement = pos=(26.8,7,12) rot=(0,0,1;0rad)
  Radius = 1.65
  SecondAngle = 0
FEATURE [Part::Cylinder] Cylinder148  label="Cilindro148"
  Angle = 360
  AttacherType = Attacher::AttachEngine3D
  FirstAngle = 0
  Height = 4
  Placement = pos=(7,7,26) rot=(0,0,1;0rad)
  Radius = 3.5
  SecondAngle = 0
FEATURE [Part::Cylinder] Cylinder149  label="Cilindro149"
  Angle = 360
  AttacherType = Attacher::AttachEngine3D
  FirstAngle = 0
  Height = 10
  Placement = pos=(21,7,25) rot=(0,0,1;0rad)
  Radius = 0.25
  SecondAngle = 0
FEATURE [Part::Cylinder] Cylinder150  label="Cilindro150"
  Angle = 360
  AttacherType = Attacher::AttachEngine3D
  FirstAngle = 0
  Height = 10
  Placement = pos=(19,7,25) rot=(0,0,1;0rad)
  Radius = 0.25
  SecondAngle = 0
FEATURE [Part::Cylinder] Cylinder151  label="Cilindro151"
  Angle = 360
  AttacherType = Attacher::AttachEngine3D
  FirstAngle = 0
  Height = 10
  Placement = pos=(17,7,25) rot=(0,0,1;0rad)
  Radius = 0.25
  SecondAngle = 0
FEATURE [Part::Cylinder] Cylinder152  label="Cilindro152"
  Angle = 360
  AttacherType = Attacher::AttachEngine3D
  FirstAngle = 0
  Height = 10
  Placement = pos=(15,7,27) rot=(0,0,1;0rad)
  Radius = 0.25
  SecondAngle = 0
FEATURE [Part::Cylinder] Cylinder153  label="Cilindro153"
  Angle = 360
  AttacherType = Attacher::AttachEngine3D
  FirstAngle = 0
  Height = 10
  Placement = pos=(13,7,27) rot=(0,0,1;0rad)
  Radius = 0.25
  SecondAngle = 0
FEATURE [Part::Cylinder] Cylinder154  label="Cilindro154"
  Angle = 360
  AttacherType = Attacher::AttachEngine3D
  FirstAngle = 0
  Height = 20
  Placement = pos=(34,-14.8,66) rot=(0,0,1;0rad)
  Radius = 1
  SecondAngle = 0
FEATURE [Part::Cylinder] Cylinder155  label="Cilindro155"
  Angle = 360
  AttacherType = Attacher::AttachEngine3D
  FirstAngle = 0
  Height = 20
  Placement = pos=(34,15.2,66) rot=(0,0,1;0rad)
  Radius = 1
  SecondAngle = 0
FEATURE [Part::Cylinder] Cylinder156  label="Cilindro156"
  Angle = 360
  AttacherType = Attacher::AttachEngine3D
  FirstAngle = 0
  Height = 100
  Placement = pos=(0,52,2) rot=(1,0,0;1.5708rad)
  Radius = 1
  SecondAngle = 0
FEATURE [Part::Cylinder] Cylinder157  label="Cilindro157"
  Angle = 360
  AttacherType = Attacher::AttachEngine3D
  FirstAngle = 0
  Height = 110
  Placement = pos=(-55,0,2) rot=(0.57735,0.57735,0.57735;2.0944rad)
  Radius = 1
  SecondAngle = 0
FEATURE [Part::Cylinder] Cylinder158  label="Cilindro158"
  Angle = 360
  AttacherType = Attacher::AttachEngine3D
  FirstAngle = 0
  Height = 29
  Placement = pos=(-15,22,112) rot=(1,0,0;1.5708rad)
  Radius = 1
  SecondAngle = 0
FEATURE [Part::Cylinder] Cylinder159  label="Cilindro159"
  Angle = 360
  AttacherType = Attacher::AttachEngine3D
  FirstAngle = 0
  Height = 29
  Placement = pos=(-5,22,112) rot=(1,0,0;1.5708rad)
  Radius = 1
  SecondAngle = 0
FEATURE [Part::Cylinder] Cylinder160  label="Cilindro160"
  Angle = 360
  AttacherType = Attacher::AttachEngine3D
  FirstAngle = 0
  Height = 29
  Placement = pos=(5,22,112) rot=(1,0,0;1.5708rad)
  Radius = 1
  SecondAngle = 0
FEATURE [Part::Cylinder] Cylinder161  label="Cilindro161"
  Angle = 360
  AttacherType = Attacher::AttachEngine3D
  FirstAngle = 0
  Height = 29
  Placement = pos=(15,22,112) rot=(1,0,0;1.5708rad)
  Radius = 1
  SecondAngle = 0
FEATURE [Part::Cylinder] Cylinder162  label="Cilindro162"
  Angle = 360
  AttacherType = Attacher::AttachEngine3D
  FirstAngle = 0
  Height = 10
  Placement = pos=(-5,-14,119) rot=(0,0,1;0rad)
  Radius = 0.75
  SecondAngle = 0
FEATURE [Part::Cylinder] Cylinder163  label="Cilindro163"
  Angle = 360
  AttacherType = Attacher::AttachEngine3D
  FirstAngle = 0
  Height = 10
  Placement = pos=(5,-14,119) rot=(0,0,1;0rad)
  Radius = 0.75
  SecondAngle = 0
FEATURE [Part::Fillet] Fillet
  Base = -> Cylinder
  EdgeLinks = -> Cylinder [Edge3]
  Edges = 1 edges r=1: [Edge3]
FEATURE [Part::Cut] Cut
  Base = -> Fillet
  Tool = -> Cylinder003
FEATURE [Part::Cut] Cut001  label="BaseInf"
  Base = -> Cut
  Tool = -> Cylinder002
FEATURE [Part::Cut] Cut093  label="BaseInf001"
  Base = -> Cut001
  Tool = -> Cylinder011
FEATURE [Part::Cut] Cut094  label="BaseInf002"
  Base = -> Cut093
  Tool = -> Box003
FEATURE [Part::Fillet] Fillet003
  Base = -> Cut118
  EdgeLinks = -> Cut118 [Edge23]
  Edges = 1 edges r=1: [Edge23]
FEATURE [Part::Fillet] Fillet004
  Base = -> Fillet003
  EdgeLinks = -> Fillet003 [Edge4]
  Edges = 1 edges r=1: [Edge4]
FEATURE [Part::Fillet] Fillet005  label="PortaSensor_Inclinacion001"
  Base = -> Fillet004
  EdgeLinks = -> Fillet004 [Edge34]
  Edges = 1 edges r=1: [Edge34]
  Placement = pos=(0,3.5,4) rot=(0,0,1;0rad)
FEATURE [Part::Fillet] Fillet006
  Base = -> Fillet005
  EdgeLinks = -> Fillet005 [Edge48]
  Edges = 1 edges r=1: [Edge48]
FEATURE [Part::Fillet] Fillet007  label="PortaSensor_TemHum"
  Base = -> Fillet006
  EdgeLinks = -> Fillet006 [Edge7,Edge18]
  Edges = 2 edges r=1: [Edge7,Edge18]
  Placement = pos=(-18,-9,137) rot=(0.57735,0.57735,-0.57735;2.0944rad)
FEATURE [Part::Fillet] Fillet009
  Base = -> Cylinder004
  EdgeLinks = -> Cylinder004 [Edge3]
  Edges = 1 edges r=1: [Edge3]
FEATURE [Part::Cut] Cut002
  Base = -> Fillet009
  Tool = -> Cylinder006
FEATURE [Part::Cut] Cut003
  Base = -> Cut002
  Placement = pos=(0,0,97) rot=(0,0,1;0rad)
  Tool = -> Cylinder005
FEATURE [Part::Fillet] Fillet010
  Base = -> Box001
  EdgeLinks = -> Box001 [Edge1,Edge3]
  Edges = 2 edges r=1.5: [Edge1,Edge3]
FEATURE [Part::Fillet] Fillet011  label="Lateral_Iz"
  Base = -> Fillet010
  EdgeLinks = -> Fillet010 [Edge17,Edge18]
  Edges = 2 edges r=1.5: [Edge17,Edge18]
FEATURE [Part::Fillet] Fillet012
  Base = -> Box002
  EdgeLinks = -> Box002 [Edge1,Edge3]
  Edges = 2 edges r=1.5: [Edge1,Edge3]
FEATURE [Part::Fillet] Fillet013  label="Lateral_De"
  Base = -> Fillet012
  EdgeLinks = -> Fillet012 [Edge17,Edge18]
  Edges = 2 edges r=1.5: [Edge17,Edge18]
  Placement = pos=(56,0,0) rot=(0,0,1;0rad)
FEATURE [Part::Fillet] Fillet019
  Base = -> Box006
  EdgeLinks = -> Box006 [Edge1,Edge3,Edge5,Edge7]
  Edges = 4 edges r=2: [Edge1,Edge3,Edge5,Edge7]
  Placement = pos=(-39,-4,0) rot=(0,0,1;0rad)
FEATURE [Part::Fillet] Fillet020
  Base = -> Box007
  EdgeLinks = -> Box007 [Edge1,Edge3,Edge5,Edge7]
  Edges = 4 edges r=2: [Edge1,Edge3,Edge5,Edge7]
  Placement = pos=(33,-4,0) rot=(0,0,1;0rad)
FEATURE [Part::Fillet] Fillet021
  Base = -> Box008
  EdgeLinks = -> Box008 [Edge1,Edge3,Edge5,Edge7]
  Edges = 4 edges r=2: [Edge1,Edge3,Edge5,Edge7]
  Placement = pos=(-39,-4,0) rot=(0,0,1;0rad)
FEATURE [Part::Cut] Cut095
  Base = -> Cut094
  Tool = -> Fillet021
FEATURE [Part::Cut] Cut096  label="BaseInf003"
  Base = -> Cut095
  Tool = -> Fillet020
FEATURE [Part::Fillet] Fillet022
  Base = -> Box009
  EdgeLinks = -> Box009 [Edge1,Edge3,Edge5,Edge7]
  Edges = 4 edges r=2: [Edge1,Edge3,Edge5,Edge7]
  Placement = pos=(33,-4,0) rot=(0,0,1;0rad)
FEATURE [Part::Fillet] Fillet032
  Base = -> Box095
  EdgeLinks = -> Box095 [Edge1,Edge3]
  Edges = 2 edges r=1.5: [Edge1,Edge3]
FEATURE [Part::Fillet] Fillet033  label="Lateral_De001"
  Base = -> Fillet032
  EdgeLinks = -> Fillet032 [Edge17,Edge18]
  Edges = 2 edges r=1.5: [Edge17,Edge18]
  Placement = pos=(56,0,0) rot=(0,0,1;0rad)
FEATURE [Part::Cut] Cut100
  Base = -> Fillet033
  Tool = -> Cylinder010
FEATURE [Part::Cut] Cut101
  Base = -> Cut100
  Tool = -> Cylinder009
FEATURE [Part::Cut] Cut102
  Base = -> Cut101
  Tool = -> Cylinder008
FEATURE [Part::Fillet] Fillet034
  Base = -> Box096
  EdgeLinks = -> Box096 [Edge1,Edge3]
  Edges = 2 edges r=1.5: [Edge1,Edge3]
FEATURE [Part::Fillet] Fillet035  label="Lateral_Iz001"
  Base = -> Fillet034
  EdgeLinks = -> Fillet034 [Edge17,Edge18]
  Edges = 2 edges r=1.5: [Edge17,Edge18]
FEATURE [Part::Cut] Cut097
  Base = -> Fillet035
  Tool = -> Cylinder071
FEATURE [Part::Cut] Cut098
  Base = -> Cut097
  Tool = -> Cylinder073
FEATURE [Part::Cut] Cut099  label="Lateral_Iz002"
  Base = -> Cut098
  Tool = -> Cylinder072
FEATURE [Part::Fillet] Fillet039
  Base = -> Box100
  EdgeLinks = -> Box100 [Edge7]
  Edges = 1 edges r=3: [Edge7]
FEATURE [Part::Cut] Cut112
  Base = -> Fillet039
  Tool = -> Cylinder085
FEATURE [Part::Fillet] Fillet040
  Base = -> Box101
  EdgeLinks = -> Box101 [Edge5]
  Edges = 1 edges r=3: [Edge5]
FEATURE [Part::Cut] Cut111
  Base = -> Fillet040
  Tool = -> Cylinder084
FEATURE [Part::Fillet] Fillet041
  Base = -> Cut111
  EdgeLinks = -> Cut111 [Edge15]
  Edges = 1 edges r=0.5: [Edge15]
  Placement = pos=(0,2,0) rot=(0,0,1;0rad)
FEATURE [Part::Fillet] Fillet042
  Base = -> Cut112
  EdgeLinks = -> Cut112 [Edge15]
  Edges = 1 edges r=0.5: [Edge15]
  Placement = pos=(0,2,0) rot=(0,0,1;0rad)
FEATURE [Part::Fillet] Fillet043
  Base = -> Cut116
  EdgeLinks = -> Cut116 [Edge23]
  Edges = 1 edges r=1: [Edge23]
FEATURE [Part::Fillet] Fillet001
  Base = -> Fillet043
  EdgeLinks = -> Fillet043 [Edge4]
  Edges = 1 edges r=1: [Edge4]
FEATURE [Part::Fillet] Fillet002  label="PortaSensor"
  Base = -> Fillet001
  EdgeLinks = -> Fillet001 [Edge34]
  Edges = 1 edges r=1: [Edge34]
  Placement = pos=(-12,11,110) rot=(0,0,1;0rad)
FEATURE [Part::Fillet] Fillet044
  Base = -> Fillet002
  EdgeLinks = -> Fillet002 [Edge48]
  Edges = 1 edges r=1: [Edge48]
FEATURE [Part::Fillet] Fillet045
  Base = -> Fillet044
  EdgeLinks = -> Fillet044 [Edge18]
  Edges = 1 edges r=1: [Edge18]
FEATURE [Part::Fillet] Fillet046
  Base = -> Fillet045
  EdgeLinks = -> Fillet045 [Edge22]
  Edges = 1 edges r=1: [Edge22]
FEATURE [Part::Fillet] Fillet049
  Base = -> Box110
  EdgeLinks = -> Box110 [Edge1,Edge3,Edge5,Edge7]
  Edges = 4 edges r=6: [Edge1,Edge3,Edge5,Edge7]
FEATURE [Part::Fillet] Fillet051
  Base = -> Box111
  EdgeLinks = -> Box111 [Edge1,Edge3]
  Edges = 2 edges r=1.5: [Edge1,Edge3]
FEATURE [Part::Fillet] Fillet052  label="Lateral_Iz006"
  Base = -> Fillet051
  EdgeLinks = -> Fillet051 [Edge17,Edge18]
  Edges = 2 edges r=1.5: [Edge17,Edge18]
FEATURE [Part::Cut] Cut120
  Base = -> Fillet052
  Tool = -> Cylinder086
FEATURE [Part::Cut] Cut121
  Base = -> Cut120
  Tool = -> Cylinder088
FEATURE [Part::Cut] Cut122  label="Lateral_Iz004"
  Base = -> Cut121
  Tool = -> Cylinder087
FEATURE [Part::Fillet] Fillet053
  Base = -> Box114
  EdgeLinks = -> Box114 [Edge1,Edge3]
  Edges = 2 edges r=1.5: [Edge1,Edge3]
FEATURE [Part::Fillet] Fillet054  label="Lateral_De005"
  Base = -> Fillet053
  EdgeLinks = -> Fillet053 [Edge17,Edge18]
  Edges = 2 edges r=1.5: [Edge17,Edge18]
  Placement = pos=(56,0,0) rot=(0,0,1;0rad)
FEATURE [Part::Cut] Cut124
  Base = -> Fillet054
  Tool = -> Cylinder091
FEATURE [Part::Cut] Cut125
  Base = -> Cut124
  Tool = -> Cylinder090
FEATURE [Part::Cut] Cut126
  Base = -> Cut125
  Tool = -> Cylinder089
FEATURE [Part::Fillet] Fillet058
  Base = -> Box118
  EdgeLinks = -> Box118 [Edge7]
  Edges = 1 edges r=3: [Edge7]
FEATURE [Part::Cut] Cut136
  Base = -> Fillet058
  Tool = -> Cylinder103
FEATURE [Part::Fillet] Fillet059
  Base = -> Box119
  EdgeLinks = -> Box119 [Edge5]
  Edges = 1 edges r=3: [Edge5]
FEATURE [Part::Cut] Cut135
  Base = -> Fillet059
  Tool = -> Cylinder102
FEATURE [Part::Fillet] Fillet060
  Base = -> Cut135
  EdgeLinks = -> Cut135 [Edge15]
  Edges = 1 edges r=0.5: [Edge15]
  Placement = pos=(0,2,0) rot=(0,0,1;0rad)
FEATURE [Part::Fillet] Fillet061
  Base = -> Cut136
  EdgeLinks = -> Cut136 [Edge15]
  Edges = 1 edges r=0.5: [Edge15]
  Placement = pos=(0,2,0) rot=(0,0,1;0rad)
FEATURE [Part::Fillet] Fillet062
  Base = -> Box120
  EdgeLinks = -> Box120 [Edge3,Edge7]
  Edges = 2 edges r=1.5: [Edge3,Edge7]
FEATURE [Part::Fillet] Fillet063
  Base = -> Fillet062
  EdgeLinks = -> Fillet062 [Edge2,Edge13]
  Edges = 2 edges r=1.5: [Edge2,Edge13]
  Placement = pos=(0,0,-3) rot=(0,0,1;0rad)
FEATURE [Part::Fillet] Fillet064
  Base = -> Box121
  EdgeLinks = -> Box121 [Edge3,Edge7]
  Edges = 2 edges r=1.5: [Edge3,Edge7]
FEATURE [Part::Fillet] Fillet065
  Base = -> Fillet064
  EdgeLinks = -> Fillet064 [Edge2,Edge13]
  Edges = 2 edges r=1.5: [Edge2,Edge13]
  Placement = pos=(0,0,-3) rot=(0,0,1;0rad)
FEATURE [Part::Fillet] Fillet069
  Base = -> Cut144
  EdgeLinks = -> Cut144 [Edge23]
  Edges = 1 edges r=1: [Edge23]
FEATURE [Part::Fillet] Fillet070
  Base = -> Fillet069
  EdgeLinks = -> Fillet069 [Edge4]
  Edges = 1 edges r=1: [Edge4]
FEATURE [Part::Fillet] Fillet071  label="PortaSensor_Inclinacion002"
  Base = -> Fillet070
  EdgeLinks = -> Fillet070 [Edge34]
  Edges = 1 edges r=1: [Edge34]
  Placement = pos=(0,3.5,4) rot=(0,0,1;0rad)
FEATURE [Part::Fillet] Fillet072
  Base = -> Fillet071
  EdgeLinks = -> Fillet071 [Edge48]
  Edges = 1 edges r=1: [Edge48]
FEATURE [Part::Fillet] Fillet073  label="PortaSensor_TemHum001"
  Base = -> Fillet072
  EdgeLinks = -> Fillet072 [Edge7,Edge18]
  Edges = 2 edges r=1: [Edge7,Edge18]
  Placement = pos=(17.5,13,140) rot=(0.57735,-0.57735,-0.57735;4.18879rad)
FEATURE [Part::Fillet] Fillet081
  Base = -> Cut150
  EdgeLinks = -> Cut150 [Edge23]
  Edges = 1 edges r=1: [Edge23]
FEATURE [Part::Fillet] Fillet082  label="PortaSensor_Inclinación"
  Base = -> Fillet081
  EdgeLinks = -> Fillet081 [Edge8]
  Edges = 1 edges r=1: [Edge8]
  Placement = pos=(-10,-11,110) rot=(1,0,0;1.5708rad)
FEATURE [Part::Fillet] Fillet083
  Base = -> Cut153
  EdgeLinks = -> Cut153 [Edge13,Edge29]
  Edges = 2 edges r=1.5: [Edge13,Edge29]
FEATURE [Part::Fillet] Fillet084  label="PortaPilas_9V"
  Base = -> Fillet083
  EdgeLinks = -> Fillet083 [Edge23,Edge41]
  Edges = 2 edges r=1.5: [Edge23,Edge41]
FEATURE [Part::Fillet] Fillet120
  Base = -> Cylinder134
  EdgeLinks = -> Cylinder134 [Edge3]
  Edges = 1 edges r=1: [Edge3]
FEATURE [Part::Cut] Cut205
  Base = -> Fillet120
  Tool = -> Cylinder136
FEATURE [Part::Cut] Cut206  label="BaseInf010"
  Base = -> Cut205
  Tool = -> Cylinder135
FEATURE [Part::Cut] Cut207  label="BaseInf011"
  Base = -> Cut206
  Tool = -> Cylinder137
FEATURE [Part::Cut] Cut208  label="BaseInf012"
  Base = -> Cut207
  Tool = -> Box170
FEATURE [Part::Fillet] Fillet121
  Base = -> Box171
  EdgeLinks = -> Box171 [Edge1,Edge3,Edge5,Edge7]
  Edges = 4 edges r=2: [Edge1,Edge3,Edge5,Edge7]
  Placement = pos=(33,-4,0) rot=(0,0,1;0rad)
FEATURE [Part::Fillet] Fillet122
  Base = -> Box172
  EdgeLinks = -> Box172 [Edge1,Edge3,Edge5,Edge7]
  Edges = 4 edges r=2: [Edge1,Edge3,Edge5,Edge7]
  Placement = pos=(-39,-4,0) rot=(0,0,1;0rad)
FEATURE [Part::Cut] Cut209
  Base = -> Cut208
  Tool = -> Fillet122
FEATURE [Part::Cut] Cut210  label="BaseInf013"
  Base = -> Cut209
  Tool = -> Fillet121
FEATURE [Part::Fillet] Fillet123
  Base = -> Box173
  EdgeLinks = -> Box173 [Edge1,Edge3]
  Edges = 2 edges r=1.5: [Edge1,Edge3]
FEATURE [Part::Fillet] Fillet124  label="Lateral_Iz010"
  Base = -> Fillet123
  EdgeLinks = -> Fillet123 [Edge17,Edge18]
  Edges = 2 edges r=1.5: [Edge17,Edge18]
FEATURE [Part::Cut] Cut211
  Base = -> Fillet124
  Tool = -> Cylinder138
FEATURE [Part::Cut] Cut212
  Base = -> Cut211
  Tool = -> Cylinder140
FEATURE [Part::Cut] Cut213  label="Lateral_Iz008"
  Base = -> Cut212
  Tool = -> Cylinder139
FEATURE [Part::Fillet] Fillet125
  Base = -> Box176
  EdgeLinks = -> Box176 [Edge1,Edge3]
  Edges = 2 edges r=1.5: [Edge1,Edge3]
FEATURE [Part::Fillet] Fillet126  label="Lateral_De009"
  Base = -> Fillet125
  EdgeLinks = -> Fillet125 [Edge17,Edge18]
  Edges = 2 edges r=1.5: [Edge17,Edge18]
  Placement = pos=(56,0,0) rot=(0,0,1;0rad)
FEATURE [Part::Cut] Cut215
  Base = -> Fillet126
  Tool = -> Cylinder143
FEATURE [Part::Cut] Cut216
  Base = -> Cut215
  Tool = -> Cylinder142
FEATURE [Part::Cut] Cut217
  Base = -> Cut216
  Tool = -> Cylinder141
FEATURE [Part::Fillet] Fillet130
  Base = -> Box180
  EdgeLinks = -> Box180 [Edge7]
  Edges = 1 edges r=3: [Edge7]
FEATURE [Part::Cut] Cut227
  Base = -> Fillet130
  Tool = -> Cylinder155
FEATURE [Part::Fillet] Fillet131
  Base = -> Box181
  EdgeLinks = -> Box181 [Edge5]
  Edges = 1 edges r=3: [Edge5]
FEATURE [Part::Cut] Cut226
  Base = -> Fillet131
  Tool = -> Cylinder154
FEATURE [Part::Fillet] Fillet132
  Base = -> Cut226
  EdgeLinks = -> Cut226 [Edge15]
  Edges = 1 edges r=0.5: [Edge15]
  Placement = pos=(0,2,0) rot=(0,0,1;0rad)
FEATURE [Part::Fillet] Fillet133
  Base = -> Cut227
  EdgeLinks = -> Cut227 [Edge15]
  Edges = 1 edges r=0.5: [Edge15]
  Placement = pos=(0,2,0) rot=(0,0,1;0rad)
FEATURE [Part::Fillet] Fillet134
  Base = -> Box182
  EdgeLinks = -> Box182 [Edge3,Edge7]
  Edges = 2 edges r=1.5: [Edge3,Edge7]
FEATURE [Part::Fillet] Fillet135
  Base = -> Fillet134
  EdgeLinks = -> Fillet134 [Edge2,Edge13]
  Edges = 2 edges r=1.5: [Edge2,Edge13]
  Placement = pos=(0,0,-3) rot=(0,0,1;0rad)
FEATURE [Part::Fillet] Fillet136
  Base = -> Box183
  EdgeLinks = -> Box183 [Edge3,Edge7]
  Edges = 2 edges r=1.5: [Edge3,Edge7]
FEATURE [Part::Fillet] Fillet137
  Base = -> Fillet136
  EdgeLinks = -> Fillet136 [Edge2,Edge13]
  Edges = 2 edges r=1.5: [Edge2,Edge13]
  Placement = pos=(0,0,-3) rot=(0,0,1;0rad)
FEATURE [Part::Fillet] Fillet145
  Base = -> Cylinder162
  EdgeLinks = -> Cylinder162 [Edge3]
  Edges = 1 edges r=0.5: [Edge3]
FEATURE [Part::Fillet] Fillet146
  Base = -> Fillet145
  EdgeLinks = -> Fillet145 [Edge3]
  Edges = 1 edges r=0.5: [Edge3]
FEATURE [Part::Fillet] Fillet147
  Base = -> Cylinder163
  EdgeLinks = -> Cylinder163 [Edge3]
  Edges = 1 edges r=0.5: [Edge3]
FEATURE [Part::Fillet] Fillet148
  Base = -> Fillet147
  EdgeLinks = -> Fillet147 [Edge3]
  Edges = 1 edges r=0.5: [Edge3]
FEATURE [Part::MultiFuse] Fusion069
  Shapes = -> [Cylinder074,Cylinder075]
FEATURE [Part::MultiFuse] Fusion070
  Shapes = -> [Box097,Fusion069]
FEATURE [Part::MultiFuse] Fusion071
  Shapes = -> [Fusion070,Box098]
FEATURE [Part::Cut] Cut103
  Base = -> Fusion071
  Tool = -> Cylinder076
FEATURE [Part::Cut] Cut104  label="Servo002"
  Base = -> Cut103
  Tool = -> Cylinder077
FEATURE [Part::MultiFuse] Fusion072
  Shapes = -> [Cylinder078,Box099]
FEATURE [Part::Fillet] Fillet036
  Base = -> Fusion072
  EdgeLinks = -> Fusion072 [Edge4]
  Edges = 1 edges r=2: [Edge4]
FEATURE [Part::Fillet] Fillet037
  Base = -> Fillet036
  EdgeLinks = -> Fillet036 [Edge25]
  Edges = 1 edges r=1: [Edge25]
FEATURE [Part::Fillet] Fillet038
  Base = -> Fillet037
  EdgeLinks = -> Fillet037 [Edge17]
  Edges = 1 edges r=1: [Edge17]
FEATURE [Part::MultiFuse] Fusion073
  Shapes = -> [Cut104,Fillet038]
FEATURE [Part::Cut] Cut105
  Base = -> Fusion073
  Tool = -> Cylinder079
FEATURE [Part::Cut] Cut106
  Base = -> Cut105
  Tool = -> Cylinder083
FEATURE [Part::Cut] Cut107
  Base = -> Cut106
  Tool = -> Cylinder082
FEATURE [Part::Cut] Cut108
  Base = -> Cut107
  Tool = -> Cylinder081
FEATURE [Part::Cut] Cut109  label="Servo003"
  Base = -> Cut108
  Placement = pos=(41,12,85) rot=(0.707107,-0.707107,0;3.14159rad)
  Tool = -> Cylinder080
FEATURE [Part::Cut] Cut110
  Base = -> Cut102
  Tool = -> Cut109
FEATURE [Part::MultiFuse] Fusion
  Shapes = -> [Cut110,Fillet041]
FEATURE [Part::MultiFuse] Fusion074  label="Lateral_De002"
  Shapes = -> [Fusion,Fillet042]
FEATURE [Part::MultiFuse] Fusion078
  Shapes = -> [Cylinder092,Cylinder093]
FEATURE [Part::MultiFuse] Fusion079
  Shapes = -> [Box115,Fusion078]
FEATURE [Part::MultiFuse] Fusion080
  Shapes = -> [Fusion079,Box116]
FEATURE [Part::Cut] Cut127
  Base = -> Fusion080
  Tool = -> Cylinder094
FEATURE [Part::Cut] Cut128  label="Servo004"
  Base = -> Cut127
  Tool = -> Cylinder095
FEATURE [Part::MultiFuse] Fusion081
  Shapes = -> [Cylinder096,Box117]
FEATURE [Part::Fillet] Fillet055
  Base = -> Fusion081
  EdgeLinks = -> Fusion081 [Edge4]
  Edges = 1 edges r=2: [Edge4]
FEATURE [Part::Fillet] Fillet056
  Base = -> Fillet055
  EdgeLinks = -> Fillet055 [Edge25]
  Edges = 1 edges r=1: [Edge25]
FEATURE [Part::Fillet] Fillet057
  Base = -> Fillet056
  EdgeLinks = -> Fillet056 [Edge17]
  Edges = 1 edges r=1: [Edge17]
FEATURE [Part::MultiFuse] Fusion082
  Shapes = -> [Cut128,Fillet057]
FEATURE [Part::Cut] Cut129
  Base = -> Fusion082
  Tool = -> Cylinder097
FEATURE [Part::Cut] Cut130
  Base = -> Cut129
  Tool = -> Cylinder101
FEATURE [Part::Cut] Cut131
  Base = -> Cut130
  Tool = -> Cylinder100
FEATURE [Part::Cut] Cut132
  Base = -> Cut131
  Tool = -> Cylinder099
FEATURE [Part::Cut] Cut133  label="Servo005"
  Base = -> Cut132
  Placement = pos=(41,12,85) rot=(0.707107,-0.707107,0;3.14159rad)
  Tool = -> Cylinder098
FEATURE [Part::Cut] Cut134
  Base = -> Cut126
  Tool = -> Cut133
FEATURE [Part::MultiFuse] Fusion077
  Shapes = -> [Cut134,Fillet060]
FEATURE [Part::MultiFuse] Fusion083  label="Lateral_De006"
  Shapes = -> [Fusion077,Fillet061]
FEATURE [Part::MultiFuse] Fusion084
  Shapes = -> [Fillet073,Box130]
FEATURE [Part::Fillet] Fillet077
  Base = -> Fusion084
  EdgeLinks = -> Fusion084 [Edge2,Edge16]
  Edges = 2 edges r=1: [Edge2,Edge16]
FEATURE [Part::Fillet] Fillet078  label="PortaSensor_TemHum002"
  Base = -> Fillet077
  EdgeLinks = -> Fillet077 [Edge20,Edge56]
  Edges = 2 edges r=1: [Edge20,Edge56]
FEATURE [Part::Fillet] Fillet079
  Base = -> Fillet078
  EdgeLinks = -> Fillet078 [Edge45]
  Edges = 1 edges r=1.5: [Edge45]
FEATURE [Part::Fillet] Fillet080  label="PortaSensor_TemHum003"
  Base = -> Fillet079
  EdgeLinks = -> Fillet079 [Edge39]
  Edges = 1 edges r=1.5: [Edge39]
  Placement = pos=(1,15.5,0) rot=(0,0,1;0rad)
FEATURE [Part::MultiFuse] Fusion097
  Shapes = -> [Cylinder144,Cylinder145]
FEATURE [Part::MultiFuse] Fusion098
  Shapes = -> [Box177,Fusion097]
FEATURE [Part::MultiFuse] Fusion099
  Shapes = -> [Fusion098,Box178]
FEATURE [Part::Cut] Cut218
  Base = -> Fusion099
  Tool = -> Cylinder146
FEATURE [Part::Cut] Cut219  label="Servo006"
  Base = -> Cut218
  Tool = -> Cylinder147
FEATURE [Part::MultiFuse] Fusion100
  Shapes = -> [Cylinder148,Box179]
FEATURE [Part::Fillet] Fillet127
  Base = -> Fusion100
  EdgeLinks = -> Fusion100 [Edge4]
  Edges = 1 edges r=2: [Edge4]
FEATURE [Part::Fillet] Fillet128
  Base = -> Fillet127
  EdgeLinks = -> Fillet127 [Edge25]
  Edges = 1 edges r=1: [Edge25]
FEATURE [Part::Fillet] Fillet129
  Base = -> Fillet128
  EdgeLinks = -> Fillet128 [Edge17]
  Edges = 1 edges r=1: [Edge17]
FEATURE [Part::MultiFuse] Fusion101
  Shapes = -> [Cut219,Fillet129]
FEATURE [Part::Cut] Cut220
  Base = -> Fusion101
  Tool = -> Cylinder149
FEATURE [Part::Cut] Cut221
  Base = -> Cut220
  Tool = -> Cylinder153
FEATURE [Part::Cut] Cut222
  Base = -> Cut221
  Tool = -> Cylinder152
FEATURE [Part::Cut] Cut223
  Base = -> Cut222
  Tool = -> Cylinder151
FEATURE [Part::Cut] Cut224  label="Servo007"
  Base = -> Cut223
  Placement = pos=(41,12,85) rot=(0.707107,-0.707107,0;3.14159rad)
  Tool = -> Cylinder150
FEATURE [Part::Cut] Cut225
  Base = -> Cut217
  Tool = -> Cut224
FEATURE [Part::MultiFuse] Fusion096
  Shapes = -> [Cut225,Fillet132]
FEATURE [Part::MultiFuse] Fusion102  label="Lateral_De010"
  Shapes = -> [Fusion096,Fillet133]
FEATURE [Part::Offset] Offset
  Fill = false
  Intersection = false
  Join = 0
  Mode = 0
  SelfIntersection = false
  Source = -> Fillet011
  Value = 0.2
FEATURE [Part::Cut] Cut004
  Base = -> Cut003
  Tool = -> Offset
FEATURE [Part::Offset] Offset001
  Fill = false
  Intersection = false
  Join = 0
  Mode = 0
  SelfIntersection = false
  Source = -> Fillet013
  Value = 0.2
FEATURE [Part::Cut] Cut005  label="Base_2"
  Base = -> Cut004
  Placement = pos=(0,0,10) rot=(0,0,1;0rad)
  Tool = -> Offset001
FEATURE [Part::Cut] Cut012
  Base = -> Cut005
  Tool = -> Fillet019
FEATURE [Part::Cut] Cut013
  Base = -> Cut012
  Tool = -> Fillet022
FEATURE [Part::MultiFuse] Fusion002  label="BaseSup"
  Shapes = -> [Cut013,Cut017]
FEATURE [Part::MultiFuse] Fusion075  label="BaseSup001"
  Shapes = -> [Fusion002,Fillet046]
FEATURE [Part::Fillet] Fillet047
  Base = -> Fusion075
  EdgeLinks = -> Fusion075 [Edge125]
  Edges = 1 edges r=2: [Edge125]
FEATURE [Part::Fillet] Fillet048
  Base = -> Fillet047
  EdgeLinks = -> Fillet047 [Edge136]
  Edges = 1 edges r=2: [Edge136]
FEATURE [Part::MultiFuse] Fusion076
  Shapes = -> [Fillet048,Fillet007]
FEATURE [Part::Chamfer] Chamfer  label="BaseSup002"
  Base = -> Fusion076
  EdgeLinks = -> Fusion076 [Edge137]
  Edges = 1 edges r=2: [Edge137]
FEATURE [Part::Cut] Cut119
  Base = -> Chamfer
  Tool = -> Fillet049
FEATURE [Part::Fillet] Fillet050  label="BaseSup003"
  Base = -> Cut119
  EdgeLinks = -> Cut119 [Edge41,Edge45]
  Edges = 2 edges r=1: [Edge41,Edge45]
FEATURE [Part::Cut] Cut147  label="BaseInf007"
  Base = -> Fillet050
  Tool = -> Box128
FEATURE [Part::Cut] Cut148
  Base = -> Cut147
  Tool = -> Box129
FEATURE [Part::Cut] Cut151  label="BaseSup004"
  Base = -> Cut148
  Tool = -> Box134
FEATURE [Part::MultiFuse] Fusion085
  Shapes = -> [Cut151,Fillet084]
FEATURE [Part::MultiFuse] Fusion086
  Shapes = -> [Fusion085,Fillet082]
FEATURE [Part::MultiFuse] Fusion087  label="BaseSup005"
  Shapes = -> [Fusion086,Fillet080]
FEATURE [Part::Cut] Cut235
  Base = -> Fusion087
  Tool = -> Box184
FEATURE [Part::Fillet] Fillet141
  Base = -> Cut235
  EdgeLinks = -> Cut235 [Edge15]
  Edges = 1 edges r=2.5: [Edge15]
FEATURE [Part::Fillet] Fillet142
  Base = -> Fillet141
  EdgeLinks = -> Fillet141 [Edge97]
  Edges = 1 edges r=2.5: [Edge97]
FEATURE [Part::Fillet] Fillet143
  Base = -> Fillet142
  EdgeLinks = -> Fillet142 [Edge20]
  Edges = 1 edges r=2.5: [Edge20]
FEATURE [Part::Fillet] Fillet144  label="BloquComponentes"
  Base = -> Fillet143
  EdgeLinks = -> Fillet143 [Edge92]
  Edges = 1 edges r=2.5: [Edge92]
FEATURE [Part::MultiFuse] Fusion103
  Shapes = -> [Fillet144,Cylinder158]
FEATURE [Part::MultiFuse] Fusion104
  Shapes = -> [Fusion103,Cylinder161]
FEATURE [Part::MultiFuse] Fusion105
  Shapes = -> [Fusion104,Cylinder160]
FEATURE [Part::MultiFuse] Fusion106
  Shapes = -> [Fusion105,Cylinder159]
FEATURE [Part::MultiFuse] Fusion107
  Shapes = -> [Fusion106,Fillet146]
FEATURE [Part::MultiFuse] Fusion108
  Shapes = -> [Fusion107,Fillet148]
FEATURE [Part::Offset] Offset002
  Fill = false
  Intersection = false
  Join = 0
  Mode = 0
  SelfIntersection = false
  Source = -> Box
  Value = 0.2
FEATURE [Part::Cut] Cut114  label="Lateral_De003"
  Base = -> Fusion074
  Tool = -> Offset002
FEATURE [Part::Cut] Cut177
  Base = -> Cut114
  Tool = -> Box165
FEATURE [Part::Cut] Cut179
  Base = -> Cut177
  Tool = -> Box167
FEATURE [Part::Cut] Cut181
  Base = -> Cut179
  Tool = -> Cylinder110
FEATURE [Part::Cut] Cut182
  Base = -> Cut181
  Tool = -> Cylinder111
FEATURE [Part::Cut] Cut183
  Base = -> Cut182
  Tool = -> Cylinder112
FEATURE [Part::Cut] Cut184
  Base = -> Cut183
  Tool = -> Cylinder120
FEATURE [Part::Cut] Cut185
  Base = -> Cut184
  Tool = -> Cylinder119
FEATURE [Part::Cut] Cut186
  Base = -> Cut185
  Tool = -> Cylinder118
FEATURE [Part::Cut] Cut187
  Base = -> Cut186
  Tool = -> Cylinder117
FEATURE [Part::Cut] Cut188
  Base = -> Cut187
  Tool = -> Cylinder116
FEATURE [Part::Cut] Cut189
  Base = -> Cut188
  Tool = -> Cylinder115
FEATURE [Part::Cut] Cut190
  Base = -> Cut189
  Tool = -> Cylinder114
FEATURE [Part::Cut] Cut191  label="LateralDer"
  Base = -> Cut190
  Tool = -> Cylinder113
FEATURE [Part::Cut] Cut202
  Base = -> Cut191
  Tool = -> Box168
FEATURE [Part::Cut] Cut203  label="LateralDer001"
  Base = -> Cut202
  Tool = -> Box169
FEATURE [Part::Cut] Cut255  label="LateralDer002"
  Base = -> Cut203
  Tool = -> Box197
FEATURE [Part::Cut] Cut256  label="LateralDer003"
  Base = -> Cut255
  Tool = -> Box198
FEATURE [Part::Offset] Offset003
  Fill = false
  Intersection = false
  Join = 0
  Mode = 0
  SelfIntersection = false
  Source = -> Box102
  Value = 0.2
FEATURE [Part::Cut] Cut113  label="Lateral_Iz003"
  Base = -> Cut099
  Tool = -> Offset003
FEATURE [Part::Cut] Cut178
  Base = -> Cut113
  Tool = -> Box166
FEATURE [Part::Cut] Cut180
  Base = -> Cut178
  Tool = -> Cylinder109
FEATURE [Part::Cut] Cut192
  Base = -> Cut180
  Tool = -> Cylinder121
FEATURE [Part::Cut] Cut193
  Base = -> Cut192
  Tool = -> Cylinder130
FEATURE [Part::Cut] Cut194
  Base = -> Cut193
  Tool = -> Cylinder129
FEATURE [Part::MultiFuse] Fusion095
  Shapes = -> [Cut194,Cylinder128]
FEATURE [Part::Cut] Cut195
  Base = -> Fusion095
  Tool = -> Cylinder127
FEATURE [Part::Cut] Cut196
  Base = -> Cut195
  Tool = -> Cylinder126
FEATURE [Part::Cut] Cut197
  Base = -> Cut196
  Tool = -> Cylinder125
FEATURE [Part::Cut] Cut198
  Base = -> Cut197
  Tool = -> Cylinder124
FEATURE [Part::Cut] Cut199
  Base = -> Cut198
  Tool = -> Cylinder123
FEATURE [Part::Cut] Cut200
  Base = -> Cut199
  Tool = -> Cylinder122
FEATURE [Part::Cut] Cut201  label="LateralIzq"
  Base = -> Cut200
  Tool = -> Cylinder131
FEATURE [Part::Offset] Offset004
  Fill = false
  Intersection = false
  Join = 0
  Mode = 0
  SelfIntersection = false
  Source = -> Box112
  Value = 0.2
FEATURE [Part::Cut] Cut123  label="Lateral_Iz005"
  Base = -> Cut122
  Tool = -> Offset004
FEATURE [Part::Cut] Cut138
  Base = -> Cut096
  Tool = -> Cut123
FEATURE [Part::Offset] Offset005
  Fill = false
  Intersection = false
  Join = 0
  Mode = 0
  SelfIntersection = false
  Source = -> Box113
  Value = 0.2
FEATURE [Part::Cut] Cut137  label="Lateral_De004"
  Base = -> Fusion083
  Tool = -> Offset005
FEATURE [Part::Cut] Cut139  label="BaseInf004"
  Base = -> Cut138
  Tool = -> Cut137
FEATURE [Part::Offset] Offset006
  Fill = false
  Intersection = false
  Join = 0
  Mode = 0
  SelfIntersection = false
  Source = -> Fillet063
  Value = 0.2
FEATURE [Part::Cut] Cut140
  Base = -> Cut139
  Tool = -> Offset006
FEATURE [Part::Offset] Offset007
  Fill = false
  Intersection = false
  Join = 0
  Mode = 0
  Placement = pos=(56,0,0) rot=(0,0,1;0rad)
  SelfIntersection = false
  Source = -> Fillet065
  Value = 0.2
FEATURE [Part::Cut] Cut141
  Base = -> Cut140
  Tool = -> Offset007
FEATURE [Part::Fillet] Fillet066
  Base = -> Cut141
  EdgeLinks = -> Cut141 [Edge55,Edge56,Edge57,Edge58,Edge59,Edge60,Edge61]
  Edges = 7 edges r=1: [Edge55,Edge56,Edge57,Edge58,Edge59,Edge60,Edge61]
FEATURE [Part::Fillet] Fillet067
  Base = -> Fillet066
  EdgeLinks = -> Fillet066 [Edge34,Edge38]
  Edges = 2 edges r=1: [Edge34,Edge38]
FEATURE [Part::Fillet] Fillet068  label="BaseInf005"
  Base = -> Fillet067
  EdgeLinks = -> Fillet067 [Edge28,Edge32]
  Edges = 2 edges r=1: [Edge28,Edge32]
FEATURE [Part::Cut] Cut142  label="BaseInf006"
  Base = -> Fillet068
  Tool = -> Cylinder104
FEATURE [Part::Cut] Cut204  label="BaseInf009"
  Base = -> Cut142
  Tool = -> Cylinder133
FEATURE [Part::Offset] Offset010
  Fill = false
  Intersection = false
  Join = 0
  Mode = 0
  SelfIntersection = false
  Source = -> Box174
  Value = 0.2
FEATURE [Part::Cut] Cut214  label="Lateral_Iz009"
  Base = -> Cut213
  Tool = -> Offset010
FEATURE [Part::Cut] Cut229
  Base = -> Cut210
  Tool = -> Cut214
FEATURE [Part::Offset] Offset011
  Fill = false
  Intersection = false
  Join = 0
  Mode = 0
  SelfIntersection = false
  Source = -> Box175
  Value = 0.2
FEATURE [Part::Cut] Cut228  label="Lateral_De008"
  Base = -> Fusion102
  Tool = -> Offset011
FEATURE [Part::Cut] Cut230  label="BaseInf014"
  Base = -> Cut229
  Tool = -> Cut228
FEATURE [Part::Offset] Offset012
  Fill = false
  Intersection = false
  Join = 0
  Mode = 0
  SelfIntersection = false
  Source = -> Fillet135
  Value = 0.2
FEATURE [Part::Cut] Cut231
  Base = -> Cut230
  Tool = -> Offset012
FEATURE [Part::Offset] Offset013
  Fill = false
  Intersection = false
  Join = 0
  Mode = 0
  Placement = pos=(56,0,0) rot=(0,0,1;0rad)
  SelfIntersection = false
  Source = -> Fillet137
  Value = 0.2
FEATURE [Part::Cut] Cut232
  Base = -> Cut231
  Tool = -> Offset013
FEATURE [Part::Fillet] Fillet138
  Base = -> Cut232
  EdgeLinks = -> Cut232 [Edge55,Edge56,Edge57,Edge58,Edge59,Edge60,Edge61]
  Edges = 7 edges r=1: [Edge55,Edge56,Edge57,Edge58,Edge59,Edge60,Edge61]
FEATURE [Part::Fillet] Fillet139
  Base = -> Fillet138
  EdgeLinks = -> Fillet138 [Edge34,Edge38]
  Edges = 2 edges r=1: [Edge34,Edge38]
FEATURE [Part::Fillet] Fillet140  label="BaseInf017"
  Base = -> Fillet139
  EdgeLinks = -> Fillet139 [Edge28,Edge32]
  Edges = 2 edges r=1: [Edge28,Edge32]
FEATURE [Part::Cut] Cut233  label="BaseInf015"
  Base = -> Fillet140
  Tool = -> Cylinder156
FEATURE [Part::Cut] Cut234  label="BaseSup012"
  Base = -> Cut233
  Placement = pos=(0,0,105) rot=(0,0,1;0rad)
  Tool = -> Cylinder157
FEATURE [Part::MultiFuse] Fusion109  label="BaseSup013"
  Shapes = -> [Cut234,Fusion108]
FEATURE [Part::MultiFuse] Fusion178  label="Capsula_Paracaidas"
  Shapes = -> [Cut201,Cut204,Fusion109,Cut256]
